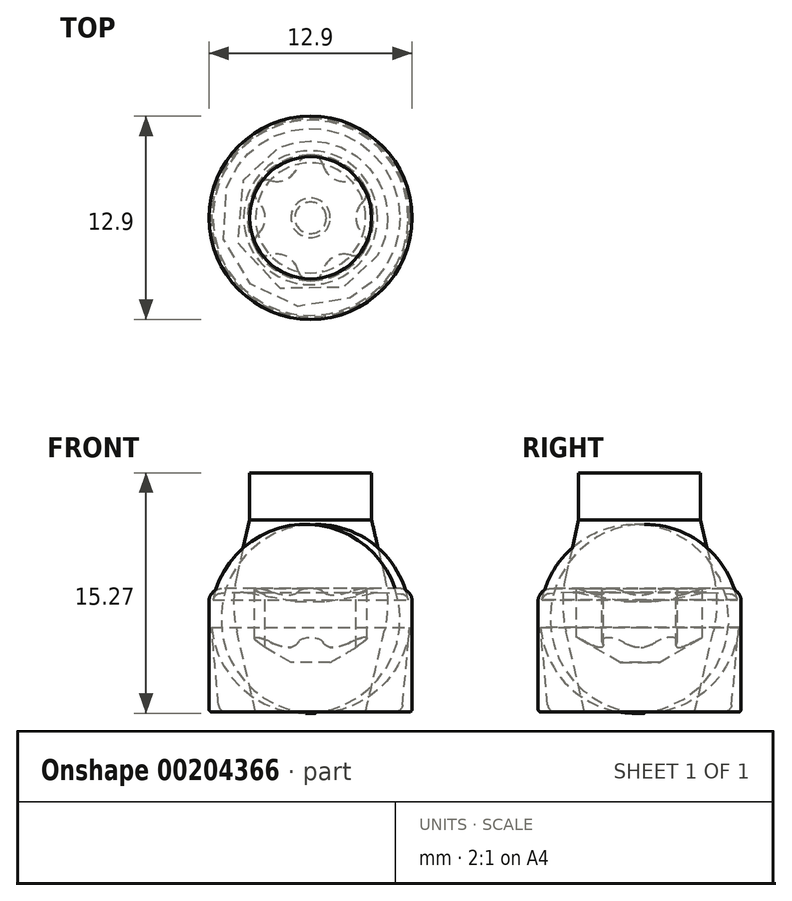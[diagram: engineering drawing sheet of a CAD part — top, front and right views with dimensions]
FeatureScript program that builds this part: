
annotation { "Feature Type Name" : "Feature", "Feature Type Description" : "" }
export const myFeature = defineFeature(function(context is Context, id is Id, definition is map)
    precondition{}
    {
        {
            var Q0;
            Q0=qCreatedBy(makeId("Front.planeOp"),FACE);
            var sketch = newSketch(context, id + "F0", { "sketchPlane" : qUnion([Q0])});
            skLineSegment(sketch, "E0", {"start": v(0, 0) * mm, "end": v(0, 3.16) * mm, "construction": true});
            skLineSegment(sketch, "E1", {"start": v(4, 7.85) * mm, "end": v(5.65, 7.85) * mm});
            skLineSegment(sketch, "E2", {"start": v(6.45, 7.05) * mm, "end": v(6.45, 0.2) * mm});
            skLineSegment(sketch, "E3", {"start": v(6.25, 0) * mm, "end": v(0, 0) * mm});
            skPoint(sketch, "E4.visualSharp", {"position": v(6.45, 7.85) * mm});
            skArc(sketch, "E4.filletArc", {"start": v(6.45, 7.05) * mm, "mid": v(6.22, 7.62) * mm, "end": v(5.65, 7.85) * mm});
            skPoint(sketch, "E5.visualSharp", {"position": v(6.45, 0) * mm});
            skArc(sketch, "E5.filletArc", {"start": v(6.25, 0) * mm, "mid": v(6.4, 0.06) * mm, "end": v(6.45, 0.2) * mm});
            skLineSegment(sketch, "E6", {"start": v(4, 7.85) * mm, "end": v(4, 4.75) * mm});
            skLineSegment(sketch, "E7", {"start": v(4, 4.75) * mm, "end": v(1.25, 3.16) * mm});
            skLineSegment(sketch, "E8", {"start": v(1.25, 3.16) * mm, "end": v(0, 3.16) * mm});
            skLineSegment(sketch, "E9", {"start": v(0, 3.16) * mm, "end": v(0, 0) * mm});
            skSolve(sketch);
        }
        {
            var Q0;
            Q0 = qSketchRegion(id + "F0", true);
            var Q1;
            Q1=sQuery(id+"F0.wireOp",EDGE,"E9");
            revolve(context, id + "F1", {"entities" : qUnion([Q0]), "axis" : qUnion([Q1]), "revolveType" : RevolveType.FULL});
        }
        {
            var Q0;
            Q0=makeQuery(id+"F1.opRevolve","SWEPT_FACE",FACE,{"disambiguationData":[OSD([sQuery(id+"F0.wireOp",EDGE,"E1")])]});
            var sketch = newSketch(context, id + "F2", { "sketchPlane" : qUnion([Q0])});
            skArc(sketch, "E10", {"start": v(0.77, 3.4) * mm, "mid": v(0, 4) * mm, "end": v(-0.77, 3.4) * mm});
            skLineSegment(sketch, "E11", {"start": v(-0.77, 3.4) * mm, "end": v(-0.79, 3.35) * mm});
            skLineSegment(sketch, "E12", {"start": v(0.77, 3.4) * mm, "end": v(0.79, 3.35) * mm});
            skLineSegment(sketch, "E13.1.0", {"start": v(-2.56, 2.37) * mm, "end": v(-2.5, 2.36) * mm});
            skArc(sketch, "E13.1.1", {"start": v(-2.56, 2.37) * mm, "mid": v(-3.46, 2) * mm, "end": v(-3.34, 1.03) * mm});
            skLineSegment(sketch, "E13.1.2", {"start": v(-3.34, 1.03) * mm, "end": v(-3.3, 0.99) * mm});
            skLineSegment(sketch, "E13.2.0", {"start": v(-3.34, -1.03) * mm, "end": v(-3.3, -0.99) * mm});
            skArc(sketch, "E13.2.1", {"start": v(-3.34, -1.03) * mm, "mid": v(-3.46, -2) * mm, "end": v(-2.56, -2.37) * mm});
            skLineSegment(sketch, "E13.2.2", {"start": v(-2.56, -2.37) * mm, "end": v(-2.5, -2.36) * mm});
            skLineSegment(sketch, "E13.3.0", {"start": v(-0.77, -3.4) * mm, "end": v(-0.79, -3.35) * mm});
            skArc(sketch, "E13.3.1", {"start": v(-0.77, -3.4) * mm, "mid": v(0, -4) * mm, "end": v(0.77, -3.4) * mm});
            skLineSegment(sketch, "E13.3.2", {"start": v(0.77, -3.4) * mm, "end": v(0.79, -3.35) * mm});
            skLineSegment(sketch, "E13.4.0", {"start": v(2.56, -2.37) * mm, "end": v(2.5, -2.36) * mm});
            skArc(sketch, "E13.4.1", {"start": v(2.56, -2.37) * mm, "mid": v(3.46, -2) * mm, "end": v(3.34, -1.03) * mm});
            skLineSegment(sketch, "E13.4.2", {"start": v(3.34, -1.03) * mm, "end": v(3.3, -0.99) * mm});
            skLineSegment(sketch, "E13.5.0", {"start": v(3.34, 1.03) * mm, "end": v(3.3, 0.99) * mm});
            skArc(sketch, "E13.5.1", {"start": v(3.34, 1.03) * mm, "mid": v(3.46, 2) * mm, "end": v(2.56, 2.37) * mm});
            skLineSegment(sketch, "E13.5.2", {"start": v(2.56, 2.37) * mm, "end": v(2.5, 2.36) * mm});
            skPoint(sketch, "E13.center", {"position": v(0, 0) * mm});
            skPoint(sketch, "E14.newPointA", {"position": v(-0.26, 1.75) * mm});
            skPoint(sketch, "E14.newPointB", {"position": v(-1.4, 1.1) * mm});
            skArc(sketch, "E14.filletArc", {"start": v(-2.5, 2.36) * mm, "mid": v(-1.44, 2.5) * mm, "end": v(-0.79, 3.35) * mm});
            skPoint(sketch, "E15.newPointA", {"position": v(0.25, 1.75) * mm});
            skPoint(sketch, "E15.newPointB", {"position": v(1.4, 1.1) * mm});
            skArc(sketch, "E15.filletArc", {"start": v(0.79, 3.35) * mm, "mid": v(1.44, 2.5) * mm, "end": v(2.5, 2.36) * mm});
            skPoint(sketch, "E16.newPointA", {"position": v(1.65, -0.65) * mm});
            skPoint(sketch, "E16.newPointB", {"position": v(1.64, 0.66) * mm});
            skArc(sketch, "E16.filletArc", {"start": v(3.3, 0.99) * mm, "mid": v(2.88, 0) * mm, "end": v(3.3, -0.99) * mm});
            skPoint(sketch, "E17.newPointA", {"position": v(0.26, -1.75) * mm});
            skPoint(sketch, "E17.newPointB", {"position": v(1.4, -1.1) * mm});
            skArc(sketch, "E17.filletArc", {"start": v(2.5, -2.36) * mm, "mid": v(1.44, -2.5) * mm, "end": v(0.79, -3.35) * mm});
            skPoint(sketch, "E18.newPointA", {"position": v(-1.4, -1.1) * mm});
            skPoint(sketch, "E18.newPointB", {"position": v(-0.25, -1.75) * mm});
            skArc(sketch, "E18.filletArc", {"start": v(-0.79, -3.35) * mm, "mid": v(-1.44, -2.5) * mm, "end": v(-2.5, -2.36) * mm});
            skPoint(sketch, "E19.newPointA", {"position": v(-1.65, 0.65) * mm});
            skPoint(sketch, "E19.newPointB", {"position": v(-1.64, -0.66) * mm});
            skArc(sketch, "E19.filletArc", {"start": v(-3.3, -0.99) * mm, "mid": v(-2.88, 0) * mm, "end": v(-3.3, 0.99) * mm});
            skCircle(sketch, "E20", {"center": v(0, 0) * mm, "radius": 4.28 * mm});
            skSolve(sketch);
        }
        {
            var Q0;
            Q0 = qSketchRegion(id + "F2", true);
            var Q1;
            Q1=makeQuery(id+"F1.opRevolve","SWEPT_FACE",FACE,{"disambiguationData":[OSD([sQuery(id+"F0.wireOp",EDGE,"E7")])]});
            extrude(context, id + "F3", {"entities" : qUnion([Q0]), "operationType" : NewBodyOperationType.ADD, "endBound" : BoundingType.UP_TO_SURFACE, "oppositeDirection" : true, "endBoundEntityFace" : qUnion([Q1]), "depth" : 25 * mm});
        }
        {
            var Q0;
            Q0=makeQuery(id+"F3.boolean.opBoolean","MERGE",FACE,{"derivedFrom":[makeQuery(id+"F1.opRevolve","SWEPT_FACE",FACE,{"disambiguationData":[OSD([sQuery(id+"F0.wireOp",EDGE,"E1")])]}),makeQuery(id+"F3.opExtrude","CAP_FACE",FACE,{"disambiguationData":[OSD([sQuery(id+"F2.wireOp",EDGE,"E10"),sQuery(id+"F2.wireOp",EDGE,"E11"),sQuery(id+"F2.wireOp",EDGE,"E12"),sQuery(id+"F2.wireOp",EDGE,"E13.1.0"),sQuery(id+"F2.wireOp",EDGE,"E13.1.1"),sQuery(id+"F2.wireOp",EDGE,"E13.1.2"),sQuery(id+"F2.wireOp",EDGE,"E13.2.0"),sQuery(id+"F2.wireOp",EDGE,"E13.2.1"),sQuery(id+"F2.wireOp",EDGE,"E13.2.2"),sQuery(id+"F2.wireOp",EDGE,"E13.3.0"),sQuery(id+"F2.wireOp",EDGE,"E13.3.1"),sQuery(id+"F2.wireOp",EDGE,"E13.3.2"),sQuery(id+"F2.wireOp",EDGE,"E13.4.0"),sQuery(id+"F2.wireOp",EDGE,"E13.4.1"),sQuery(id+"F2.wireOp",EDGE,"E13.4.2"),sQuery(id+"F2.wireOp",EDGE,"E13.5.0"),sQuery(id+"F2.wireOp",EDGE,"E13.5.1"),sQuery(id+"F2.wireOp",EDGE,"E13.5.2"),sQuery(id+"F2.wireOp",EDGE,"E14.filletArc"),sQuery(id+"F2.wireOp",EDGE,"E15.filletArc"),sQuery(id+"F2.wireOp",EDGE,"E16.filletArc"),sQuery(id+"F2.wireOp",EDGE,"E17.filletArc"),sQuery(id+"F2.wireOp",EDGE,"E18.filletArc"),sQuery(id+"F2.wireOp",EDGE,"E19.filletArc"),sQuery(id+"F2.wireOp",EDGE,"E20")])],"isStart":true})]});
            var sketch = newSketch(context, id + "F4", { "sketchPlane" : qUnion([Q0])});
            skCircle(sketch, "E21", {"center": v(0, 0) * mm, "radius": 4 * mm});
            skSolve(sketch);
        }
        {
            var Q0;
            Q0 = qSketchRegion(id + "F4", true);
            extrude(context, id + "F5", {"entities" : qUnion([Q0]), "operationType" : NewBodyOperationType.REMOVE, "oppositeDirection" : true, "depth" : 1 * mm, "hasDraft" : true, "draftAngle" : 70 * degree, "draftPullDirection" : true});
        }
        {
            var Q0;
            Q0=qCreatedBy(makeId("Front.planeOp"),FACE);
            var sketch = newSketch(context, id + "F6", { "sketchPlane" : qUnion([Q0])});
            skLineSegment(sketch, "E22", {"start": v(0, 0) * mm, "end": v(0, 15.2) * mm, "construction": true});
            skLineSegment(sketch, "E23", {"start": v(0, 15.2) * mm, "end": v(3.87, 15.2) * mm});
            skLineSegment(sketch, "E24", {"start": v(3.87, 15.2) * mm, "end": v(3.87, 12.2) * mm});
            skLineSegment(sketch, "E25", {"start": v(3.87, 12.2) * mm, "end": v(4.68, 8.72) * mm});
            skLineSegment(sketch, "E26", {"start": v(3.5, 0) * mm, "end": v(0, 0) * mm});
            skLineSegment(sketch, "E27", {"start": v(0, 15.2) * mm, "end": v(0, 0) * mm});
            skLineSegment(sketch, "E28", {"start": v(3.5, 0) * mm, "end": v(4.68, 5.12) * mm});
            skArc(sketch, "E29.filletArc", {"start": v(4.68, 5.12) * mm, "mid": v(4.88, 6.92) * mm, "end": v(4.68, 8.72) * mm});
            skSolve(sketch);
        }
        {
            var Q0;
            Q0 = qSketchRegion(id + "F6", true);
            var Q1;
            Q1=sQuery(id+"F6.wireOp",EDGE,"E27");
            revolve(context, id + "F7", {"entities" : qUnion([Q0]), "axis" : qUnion([Q1]), "revolveType" : RevolveType.FULL});
        }
        {
            var Q0;
            Q0=qCreatedBy(makeId("Front.planeOp"),FACE);
            var sketch = newSketch(context, id + "F8", { "sketchPlane" : qUnion([Q0])});
            skLineSegment(sketch, "E30", {"start": v(0, 0) * mm, "end": v(0, 7.03) * mm});
            skLineSegment(sketch, "E31", {"start": v(6.3, 5.39) * mm, "end": v(5.84, 0.45) * mm});
            skLineSegment(sketch, "E32", {"start": v(5.34, 0) * mm, "end": v(0, 0) * mm});
            skPoint(sketch, "E33.visualSharp", {"position": v(5.8, 0) * mm});
            skArc(sketch, "E33.filletArc", {"start": v(5.34, 0) * mm, "mid": v(5.68, 0.13) * mm, "end": v(5.84, 0.45) * mm});
            skLineSegment(sketch, "E34", {"start": v(0, 7.03) * mm, "end": v(0, 0) * mm, "construction": true});
            skLineSegment(sketch, "E35", {"start": v(0, 7.03) * mm, "end": v(1, 7.03) * mm});
            skLineSegment(sketch, "E36", {"start": v(1, 7.03) * mm, "end": v(4.25, 7.6) * mm});
            skLineSegment(sketch, "E37", {"start": v(4.25, 7.6) * mm, "end": v(5.74, 7.52) * mm});
            skArc(sketch, "E38.filletArc", {"start": v(6.3, 5.39) * mm, "mid": v(6.31, 6.26) * mm, "end": v(6.2, 7.12) * mm});
            skPoint(sketch, "E39.visualSharp", {"position": v(6.11, 7.5) * mm});
            skArc(sketch, "E39.filletArc", {"start": v(6.2, 7.12) * mm, "mid": v(6.04, 7.4) * mm, "end": v(5.74, 7.52) * mm});
            skLineSegment(sketch, "E40", {"start": v(6.3, 5.39) * mm, "end": v(6.35, 6) * mm, "construction": true});
            skSolve(sketch);
        }
        {
            var Q0;
            Q0 = qSketchRegion(id + "F8", true);
            var Q1;
            Q1=sQuery(id+"F8.wireOp",EDGE,"E30");
            revolve(context, id + "F9", {"entities" : qUnion([Q0]), "axis" : qUnion([Q1]), "revolveType" : RevolveType.FULL});
        }
    });
